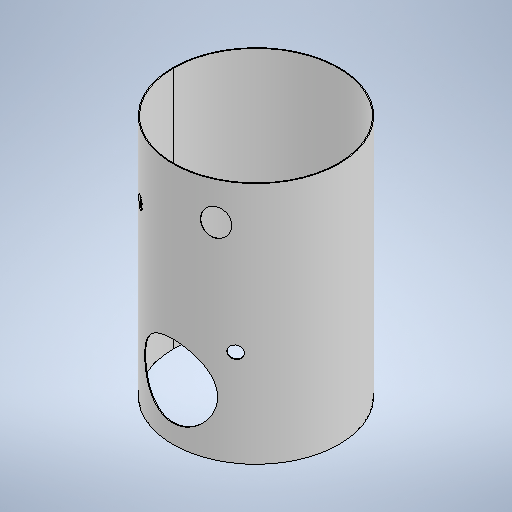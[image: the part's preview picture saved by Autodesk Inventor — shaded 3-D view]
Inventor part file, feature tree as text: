
AUTODESK INVENTOR PART (.ipt)
format: ipt  version: 2025.1 (Build 291241020, 241B)  size: 1,789,952 bytes
history: native  units: mm
features: other x9, sketch x6, extrude x4, revolve x1, plane x1
ambient origin geometry x8: Origin, YZ Plane, XZ Plane, XY Plane, X Axis, Y Axis, Z Axis, Center Point
bodies: Solid1 (feature_tree)
feature tree (21):
  revolve  "Revolution1"  [1 undecoded]
  extrude  "Extrusion1"  Depth=62.8144mm
  other  "floor angle sketch"
  other  "Feeder Plane"
  other  "Feeder horisont hight angle"
  other  "Feeder Work Plane"
  extrude  "Feeder Extrusion"  TaperAngle=0.0deg  [1 undecoded]
  other  "Inner Plane"
  other  "Inner horisont hight angle"
  other  "Inner Work Plane"
  extrude  "Inner Extrusion"  Depth=400.0mm
  other  "Outer Plane"
  sketch  "Sketch11"  dims[d16=400.0mm d17=180.0mm]
  plane  "Work Plane9"
  extrude  "Extrusion6"  Depth=400.0mm
  sketch  "Sketch1"  dims[d0=6.0mm d1=1770.0mm]
  sketch  "Sketch2"  dims[d2=1200.0mm d3=62.8144mm]
  sketch  "Sketch8"  dims[d4=530.0mm d10=0.0mm d11=0.0mm]
  sketch  "Sketch10"  dims[d12=400.0mm d15=200.0mm]
  sketch  "Sketch12"  dims[d34=1500.0mm d35=30.0deg d36=172.0mm d38=10.0mm d39=0.0mm d40=0.0mm d41=1300.0mm d42=91.0mm d43=0.0mm d44=0.0mm d45=0.0mm d46=700.0mm d47=92.0mm d48=10.0mm d49=0.0mm]
  other  "Definition1"
note: 2 required parameter values undecoded (feature->parameter linkage not recoverable at this tier; creation-order binding heuristic only, values carry confidence <= 0.55)